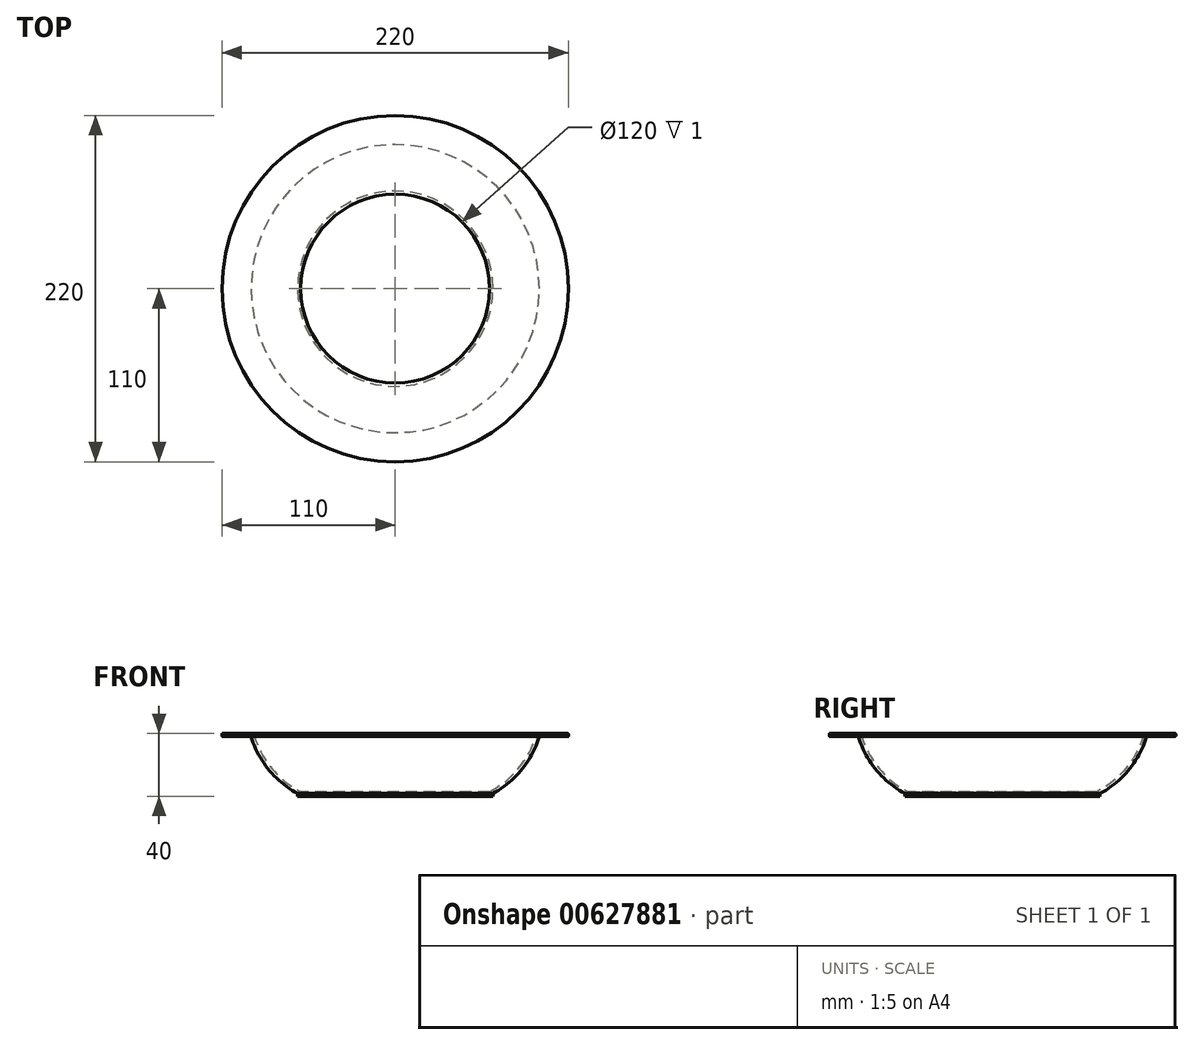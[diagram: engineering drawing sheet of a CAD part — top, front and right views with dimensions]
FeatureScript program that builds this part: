
annotation { "Feature Type Name" : "Feature", "Feature Type Description" : "" }
export const myFeature = defineFeature(function(context is Context, id is Id, definition is map)
    precondition{}
    {
        {
            var Q0;
            Q0=qCreatedBy(makeId("Front.planeOp"),FACE);
            var sketch = newSketch(context, id + "F0", { "sketchPlane" : qUnion([Q0])});
            skLineSegment(sketch, "E0.top", {"start": v(-110, 38) * mm, "end": v(-90, 38) * mm});
            skLineSegment(sketch, "E1.left", {"start": v(-60, 1) * mm, "end": v(-60, 0) * mm});
            skArc(sketch, "E2", {"start": v(-90, 38) * mm, "mid": v(-78.84, 16.38) * mm, "end": v(-60, 1) * mm});
            skLineSegment(sketch, "E3", {"start": v(-60, 0) * mm, "end": v(0, 0) * mm});
            skLineSegment(sketch, "E4.0", {"start": v(-62, -2) * mm, "end": v(0, -2) * mm});
            skLineSegment(sketch, "E4.1", {"start": v(-62, -0.2) * mm, "end": v(-62, -2) * mm});
            skArc(sketch, "E4.2", {"start": v(-91.5, 36) * mm, "mid": v(-80.3, 15) * mm, "end": v(-62, -0.2) * mm});
            skLineSegment(sketch, "E4.3", {"start": v(-110, 36) * mm, "end": v(-91.5, 36) * mm});
            skLineSegment(sketch, "E5", {"start": v(-110, 38) * mm, "end": v(-110, 36) * mm});
            skLineSegment(sketch, "E6", {"start": v(0, 0) * mm, "end": v(0, -2) * mm});
            skSolve(sketch);
        }
        {
            var Q0;
            Q0=qSketchRegion(id+"F0",true);
            var Q1;
            Q1=sQuery(id+"F0.wireOp",EDGE,"E6");
            revolve(context, id + "F1", {"entities" : qUnion([Q0]), "axis" : qUnion([Q1]), "revolveType" : RevolveType.FULL});
        }
        {
            var Q0;
            Q0=makeQuery(id+"F1.opRevolve","SWEPT_EDGE",EDGE,{"disambiguationData":[OSD([sQuery(id+"F0.wireOp",EDGE,"E4.3"),sQuery(id+"F0.wireOp",EDGE,"E5")])]});
            var Q1;
            Q1=makeQuery(id+"F1.opRevolve","SWEPT_EDGE",EDGE,{"disambiguationData":[OSD([sQuery(id+"F0.wireOp",EDGE,"E0.top"),sQuery(id+"F0.wireOp",EDGE,"E5")])]});
            var Q2;
            Q2=makeQuery(id+"F1.opRevolve","SWEPT_EDGE",EDGE,{"disambiguationData":[OSD([sQuery(id+"F0.wireOp",EDGE,"E0.top"),sQuery(id+"F0.wireOp",EDGE,"E2")])]});
            fillet(context, id + "F2", {"entities" : qUnion([Q0, Q1, Q2]), "radius" : 0.5 * mm, "tangentPropagation" : true, "allowEdgeOverflow" : false});
        }
    });
